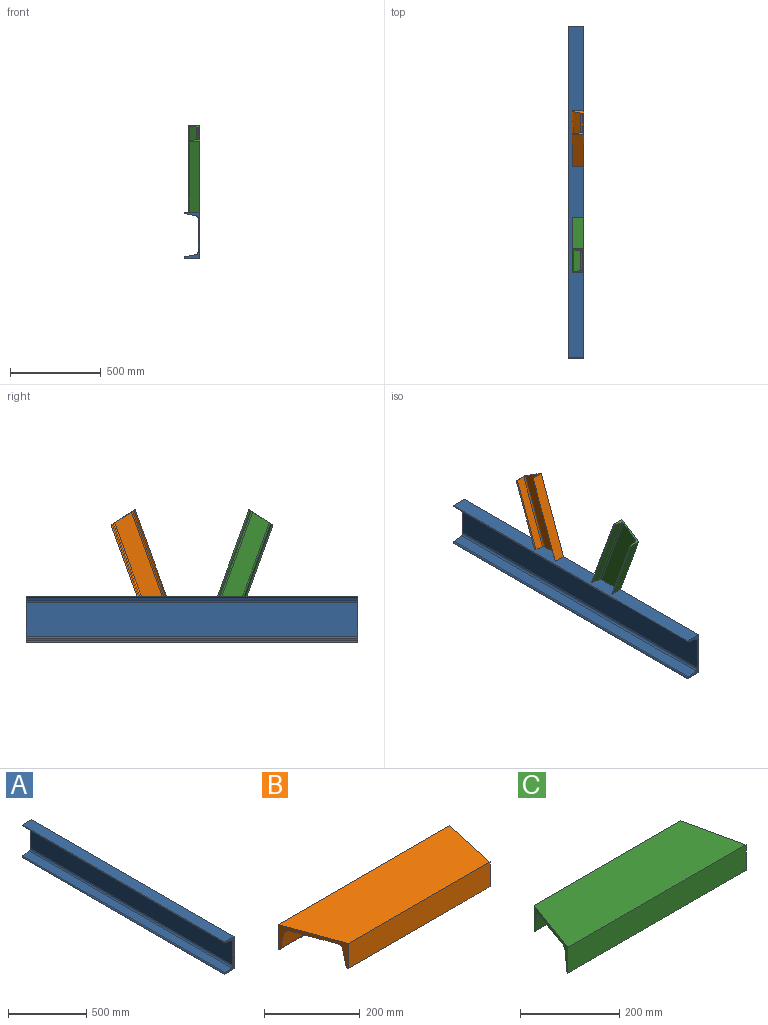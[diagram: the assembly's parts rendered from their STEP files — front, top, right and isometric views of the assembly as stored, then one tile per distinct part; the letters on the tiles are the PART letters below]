
ASSEMBLY  parts=3 mates=2
PART A: 12 faces, bbox 85.7x1828.8x254 mm
  f0: plane 1828.8x56.56mm, normal (-0.17,0,0.98), area 105033mm2, adj f1,f9,f10,f11
  f1: cylinder r=9.13mm len=1828.8mm, axis (0,1,0), area 23330.5mm2, adj f0,f2,f10,f11
  f2: plane 1828.8x85.73mm, normal (0,0,-1), area 156773.9mm2, adj f1,f3,f10,f11
  f3: plane 1828.8x254mm, normal (1,0,0), area 464515.2mm2, adj f2,f4,f10,f11
  f4: plane 1828.8x85.73mm, normal (0,0,1), area 156773.9mm2, adj f3,f5,f10,f11
  f5: cylinder r=9.13mm len=1828.8mm, axis (0,1,0), area 23330.5mm2, adj f4,f6,f10,f11
  f6: plane 1828.8x56.56mm, normal (-0.17,0,-0.98), area 105033mm2, adj f5,f7,f10,f11
  f7: cylinder r=14.62mm len=1828.8mm, axis (0,1,0), area 37331.5mm2, adj f6,f8,f10,f11
  f8: plane 1828.8x187.32mm, normal (-1,0,0), area 342577.9mm2, adj f7,f9,f10,f11
  f9: cylinder r=14.62mm len=1828.8mm, axis (0,1,0), area 37331.5mm2, adj f0,f8,f10,f11
  f10: plane 254x85.73mm, normal (0,-1,0), area 4645.8mm2, adj f0,f1,f2,f3,f4,f5,f6,f7
  f11: plane 254x85.73mm, normal (0,1,0), area 4645.8mm2, adj f0,f1,f2,f3,f4,f5,f6,f7
PART B: 12 faces, bbox 506.4x152.4x63.4 mm
  f0: plane 506.41x152.4mm, normal (0,0,1), area 70374.7mm2, adj f1,f9,f10,f11
  f1: plane 417.14x63.42mm, normal (0,-1,0), area 26456.6mm2, adj f0,f2,f10,f11
  f2: cylinder r=5.63mm len=420.39mm, axis (-1,0,0), area 3301.5mm2, adj f1,f3,f10,f11
  f3: plane 424.8x43.19mm, normal (0,0.99,-0.17), area 18527.2mm2, adj f2,f4,f10,f11
  f4: cylinder r=9.29mm len=430.16mm, axis (-1,0,0), area 5543.7mm2, adj f3,f5,f10,f11
  f5: plane 493.39x107.95mm, normal (0,0,-1), area 49850.1mm2, adj f4,f6,f10,f11
  f6: cylinder r=9.29mm len=498.75mm, axis (-1,0,0), area 6448.5mm2, adj f5,f7,f10,f11
  f7: plane 503.16x43.19mm, normal (0,-0.99,-0.17), area 21962.7mm2, adj f6,f8,f10,f11
  f8: cylinder r=5.63mm len=506.41mm, axis (-1,0,0), area 3973.9mm2, adj f7,f9,f10,f11
  f9: plane 506.41x63.42mm, normal (0,1,0), area 32118.6mm2, adj f0,f8,f10,f11
  f10: plane 152.4x63.42mm, normal (0.98,-0.22,0), area 2334mm2, adj f0,f1,f2,f3,f4,f5,f6,f7
  f11: plane 152.4x63.42mm, normal (-0.94,-0.34,0), area 2426.8mm2, adj f0,f1,f2,f3,f4,f5,f6,f7
PART C: 12 faces, bbox 506.4x152.4x63.4 mm
  f0: plane 506.41x152.4mm, normal (0,0,1), area 70374.7mm2, adj f1,f9,f10,f11
  f1: plane 417.14x63.42mm, normal (0,1,0), area 26456.6mm2, adj f0,f8,f10,f11
  f2: cylinder r=5.63mm len=506.41mm, axis (-1,0,0), area 3973.9mm2, adj f3,f9,f10,f11
  f3: plane 503.16x43.19mm, normal (0,0.99,-0.17), area 21962.7mm2, adj f2,f4,f10,f11
  f4: cylinder r=9.29mm len=498.75mm, axis (-1,0,0), area 6448.5mm2, adj f3,f5,f10,f11
  f5: plane 493.39x107.95mm, normal (0,0,-1), area 49850.1mm2, adj f4,f6,f10,f11
  f6: cylinder r=9.29mm len=430.16mm, axis (-1,0,0), area 5543.7mm2, adj f5,f7,f10,f11
  f7: plane 424.8x43.19mm, normal (0,-0.99,-0.17), area 18527.2mm2, adj f6,f8,f10,f11
  f8: cylinder r=5.63mm len=420.39mm, axis (-1,0,0), area 3301.5mm2, adj f1,f7,f10,f11
  f9: plane 506.41x63.42mm, normal (0,-1,0), area 32118.6mm2, adj f0,f2,f10,f11
  f10: plane 152.4x63.42mm, normal (0.98,0.22,0), area 2334mm2, adj f0,f1,f2,f3,f4,f5,f6,f7
  f11: plane 152.4x63.42mm, normal (-0.94,0.34,0), area 2426.8mm2, adj f0,f1,f2,f3,f4,f5,f6,f7
PLACE A t=(2590.8,3241.68,-4225.93)mm fixed
PLACE B rot(axis=(0.7,0.12,0.7),165.8deg) t=(2590.8,2539.01,-4125.08)mm
PLACE C rot(axis=(-0.7,0.12,-0.7),165.8deg) t=(2590.8,2115.54,-4125.08)mm
MATE fastened B.f11 <-> A.f4  axis (0,0,-1) through (2590.8,2629.69,-4098.92)mm
MATE fastened C.f11 <-> A.f4  axis (0,0,-1) through (2590.8,2024.86,-4098.93)mm
